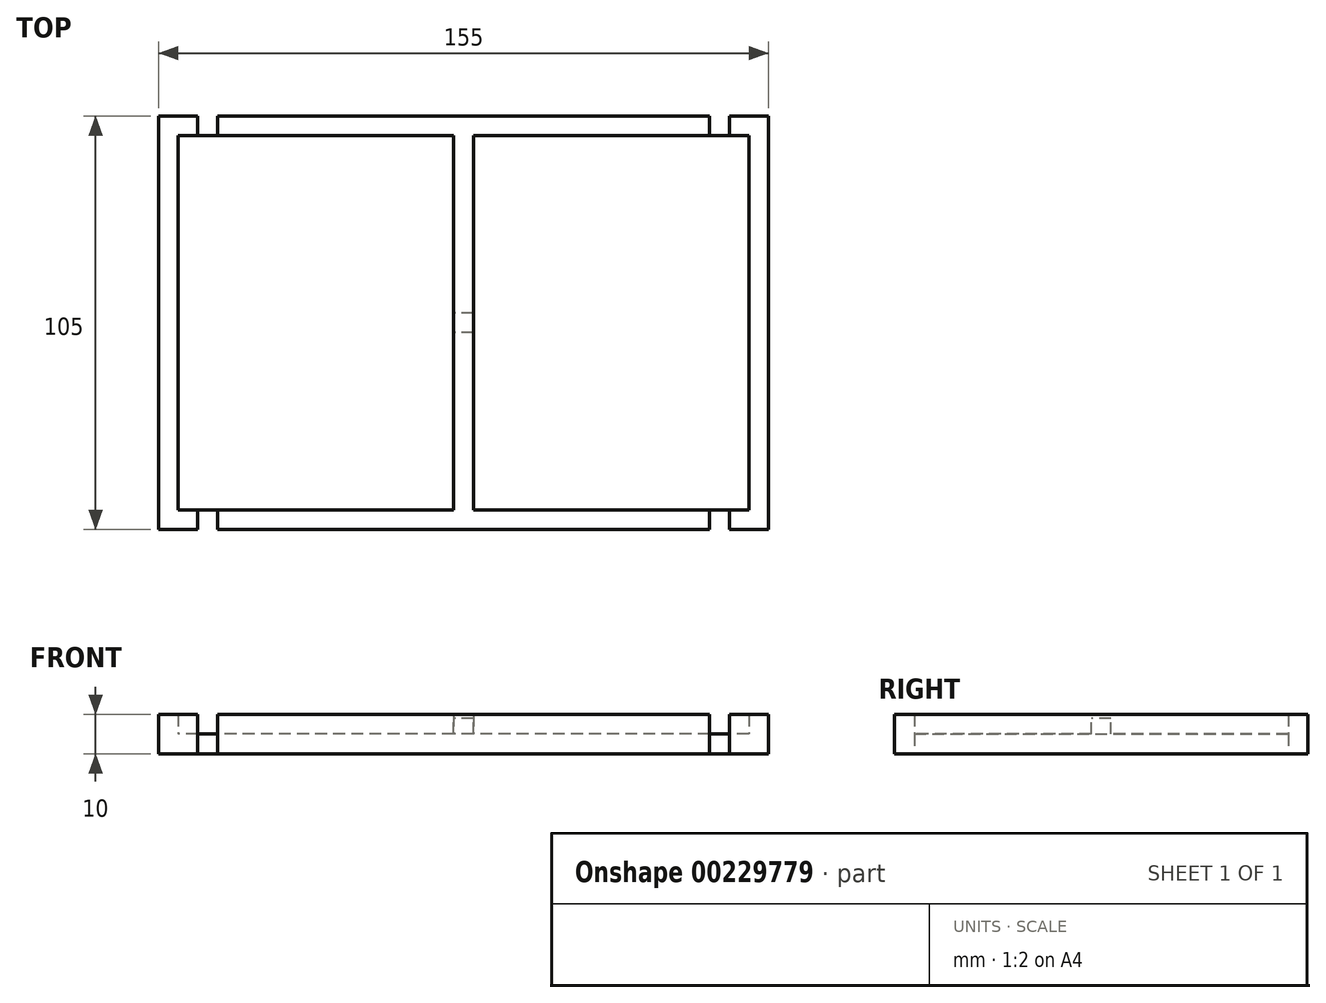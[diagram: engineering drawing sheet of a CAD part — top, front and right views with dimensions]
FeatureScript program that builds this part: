
annotation { "Feature Type Name" : "Feature", "Feature Type Description" : "" }
export const myFeature = defineFeature(function(context is Context, id is Id, definition is map)
    precondition{}
    {
        {
            var Q0;
            Q0=qCreatedBy(makeId("Top.planeOp"),FACE);
            var sketch = newSketch(context, id + "F0", { "sketchPlane" : qUnion([Q0])});
            skLineSegment(sketch, "E0.bottom", {"start": v(77.5, -52.5) * mm, "end": v(-77.5, -52.5) * mm});
            skLineSegment(sketch, "E0.top", {"start": v(77.5, 52.5) * mm, "end": v(-77.5, 52.5) * mm});
            skLineSegment(sketch, "E0.left", {"start": v(77.5, -52.5) * mm, "end": v(77.5, 52.5) * mm});
            skLineSegment(sketch, "E0.right", {"start": v(-77.5, -52.5) * mm, "end": v(-77.5, 52.5) * mm});
            skPoint(sketch, "E0.middle", {"position": v(0, 0) * mm});
            skLineSegment(sketch, "E1.bottom", {"start": v(2.5, -52.5) * mm, "end": v(-2.5, -52.5) * mm});
            skLineSegment(sketch, "E1.top", {"start": v(2.5, 52.5) * mm, "end": v(-2.5, 52.5) * mm});
            skLineSegment(sketch, "E1.left", {"start": v(2.5, -52.5) * mm, "end": v(2.5, 52.5) * mm});
            skLineSegment(sketch, "E1.right", {"start": v(-2.5, -52.5) * mm, "end": v(-2.5, 52.5) * mm});
            skSolve(sketch);
        }
        {
            var Q0;
            {var subQ0=sQuery(id+"F0.wireOp",EDGE,"E0.left");Q0=makeQuery(id+"F0.imprint","IMPRINT",FACE,{"disambiguationData":[TD([[makeQuery(id+"F0.imprint","IMPRINT",EDGE,{"derivedFrom":subQ0}),1.0]])]});}
            var Q1;
            {var subQ2=sQuery(id+"F0.wireOp",EDGE,"E0.right");Q1=makeQuery(id+"F0.imprint","IMPRINT",FACE,{"disambiguationData":[TD([[makeQuery(id+"F0.imprint","IMPRINT",EDGE,{"derivedFrom":subQ2}),-1.0]])]});}
            var Q2;
            {var subQ2=sQuery(id+"F0.wireOp",EDGE,"E1.left");Q2=makeQuery(id+"F0.imprint","IMPRINT",FACE,{"disambiguationData":[TD([[makeQuery(id+"F0.imprint","IMPRINT",EDGE,{"derivedFrom":subQ2}),1.0]])]});}
            extrude(context, id + "F1", {"entities" : qUnion([Q0, Q1, Q2]), "depth" : 10 * mm, "offsetDistance" : 25 * mm});
        }
        {
            var Q0;
            Q0=makeQuery(id+"F1.opExtrude","CAP_FACE",FACE,{"disambiguationData":[OSD([sQuery(id+"F0.wireOp",EDGE,"E0.bottom"),sQuery(id+"F0.wireOp",EDGE,"E0.top"),sQuery(id+"F0.wireOp",EDGE,"E0.left"),sQuery(id+"F0.wireOp",EDGE,"E0.right")])],"isStart":false});
            shell(context, id + "F2", {"entities" : qUnion([Q0]), "thickness" : 5 * mm});
        }
        {
            var Q0;
            Q0=qCreatedBy(makeId("Top.planeOp"),FACE);
            var sketch = newSketch(context, id + "F3", { "sketchPlane" : qUnion([Q0])});
            skLineSegment(sketch, "E2.bottom", {"start": v(-77.5, 52.5) * mm, "end": v(77.5, 52.5) * mm});
            skLineSegment(sketch, "E2.top", {"start": v(-77.5, -52.5) * mm, "end": v(77.5, -52.5) * mm});
            skLineSegment(sketch, "E2.left", {"start": v(-77.5, 52.5) * mm, "end": v(-77.5, -52.5) * mm});
            skLineSegment(sketch, "E2.right", {"start": v(77.5, 52.5) * mm, "end": v(77.5, -52.5) * mm});
            skLineSegment(sketch, "E3.bottom", {"start": v(-67.5, 52.5) * mm, "end": v(-62.5, 52.5) * mm});
            skLineSegment(sketch, "E3.top", {"start": v(-67.5, 47.5) * mm, "end": v(-62.5, 47.5) * mm});
            skLineSegment(sketch, "E3.left", {"start": v(-67.5, 52.5) * mm, "end": v(-67.5, 47.5) * mm});
            skLineSegment(sketch, "E3.right", {"start": v(-62.5, 52.5) * mm, "end": v(-62.5, 47.5) * mm});
            skLineSegment(sketch, "E4.0.1.0", {"start": v(-62.5, -47.5) * mm, "end": v(-62.5, -52.5) * mm});
            skLineSegment(sketch, "E4.0.1.1", {"start": v(-67.5, -47.5) * mm, "end": v(-67.5, -52.5) * mm});
            skLineSegment(sketch, "E4.0.1.2", {"start": v(-67.5, -52.5) * mm, "end": v(-62.5, -52.5) * mm});
            skLineSegment(sketch, "E4.direction2", {"start": v(-62.5, -47.5) * mm, "end": v(-62.5, -52.5) * mm, "construction": true});
            skPoint(sketch, "E5.orphan", {"position": v(67, 54) * mm});
            skLineSegment(sketch, "E6.MirrorCS", {"start": v(62.5, 52.5) * mm, "end": v(62.5, 47.5) * mm});
            skLineSegment(sketch, "E7.MirrorCS", {"start": v(67.5, 52.5) * mm, "end": v(67.5, 47.5) * mm});
            skLineSegment(sketch, "E8.MirrorCS", {"start": v(67.5, 52.5) * mm, "end": v(62.5, 52.5) * mm});
            skLineSegment(sketch, "E9.MirrorCS", {"start": v(67.5, 47.5) * mm, "end": v(62.5, 47.5) * mm});
            skLineSegment(sketch, "E10.MirrorCS", {"start": v(67.5, -47.5) * mm, "end": v(67.5, -52.5) * mm});
            skLineSegment(sketch, "E11", {"start": v(-67.5, -47.5) * mm, "end": v(-62.5, -47.5) * mm});
            skLineSegment(sketch, "E12.MirrorCS", {"start": v(67.5, -47.5) * mm, "end": v(62.5, -47.5) * mm});
            skLineSegment(sketch, "E13.MirrorCS", {"start": v(62.5, -47.5) * mm, "end": v(62.5, -52.5) * mm, "construction": true});
            skLineSegment(sketch, "E14", {"start": v(62.5, -47.5) * mm, "end": v(62.5, -52.5) * mm});
            skLineSegment(sketch, "E15", {"start": v(62.5, -52.5) * mm, "end": v(67.5, -52.5) * mm});
            skSolve(sketch);
        }
        {
            var Q0;
            {var subQ0=sQuery(id+"F3.wireOp",EDGE,"E2.left");Q0=makeQuery(id+"F3.imprint","IMPRINT",FACE,{"disambiguationData":[TD([[makeQuery(id+"F3.imprint","IMPRINT",EDGE,{"derivedFrom":subQ0}),1.0]])]});}
            extrude(context, id + "F4", {"entities" : qUnion([Q0]), "operationType" : NewBodyOperationType.INTERSECT, "depth" : 25 * mm, "offsetDistance" : 25 * mm});
        }
        {
            var Q0;
            {var subQ2=sQuery(id+"F0.wireOp",EDGE,"E1.left");Q0=makeQuery(id+"F0.imprint","IMPRINT",FACE,{"disambiguationData":[TD([[makeQuery(id+"F0.imprint","IMPRINT",EDGE,{"derivedFrom":subQ2}),1.0]])]});}
            extrude(context, id + "F5", {"entities" : qUnion([Q0]), "operationType" : NewBodyOperationType.ADD, "depth" : 10 * mm, "offsetDistance" : 25 * mm});
        }
        {
            var Q0;
            Q0=makeQuery(id+"F5.opExtrude","SWEPT_FACE",FACE,{"disambiguationData":[OSD([sQuery(id+"F0.wireOp",EDGE,"E1.right")])]});
            var sketch = newSketch(context, id + "F6", { "sketchPlane" : qUnion([Q0])});
            skLineSegment(sketch, "E16.bottom", {"start": v(-47.5, 10) * mm, "end": v(47.5, 10) * mm});
            skLineSegment(sketch, "E16.top", {"start": v(-47.5, 5) * mm, "end": v(47.5, 5) * mm});
            skLineSegment(sketch, "E16.left", {"start": v(-47.5, 10) * mm, "end": v(-47.5, 5) * mm});
            skLineSegment(sketch, "E16.right", {"start": v(47.5, 10) * mm, "end": v(47.5, 5) * mm});
            skLineSegment(sketch, "E17", {"start": v(0, 10) * mm, "end": v(0, 5) * mm});
            skLineSegment(sketch, "E18.bottom", {"start": v(-2.5, 5) * mm, "end": v(2.5, 5) * mm});
            skLineSegment(sketch, "E18.top", {"start": v(-2.5, 9) * mm, "end": v(2.5, 9) * mm});
            skLineSegment(sketch, "E18.left", {"start": v(-2.5, 5) * mm, "end": v(-2.5, 9) * mm});
            skLineSegment(sketch, "E18.right", {"start": v(2.5, 5) * mm, "end": v(2.5, 9) * mm});
            skPoint(sketch, "E19", {"position": v(0, 9) * mm});
            skSolve(sketch);
        }
        {
            var Q0;
            {var subQ5=sQuery(id+"F6.wireOp",EDGE,"E18.left");Q0=makeQuery(id+"F6.imprint","IMPRINT",FACE,{"disambiguationData":[TD([[makeQuery(id+"F6.imprint","IMPRINT",EDGE,{"derivedFrom":subQ5}),-1.0]])]});}
            var Q1;
            {var subQ5=sQuery(id+"F6.wireOp",EDGE,"E18.right");Q1=makeQuery(id+"F6.imprint","IMPRINT",FACE,{"disambiguationData":[TD([[makeQuery(id+"F6.imprint","IMPRINT",EDGE,{"derivedFrom":subQ5}),1.0]])]});}
            extrude(context, id + "F7", {"entities" : qUnion([Q0, Q1]), "operationType" : NewBodyOperationType.REMOVE, "oppositeDirection" : true, "depth" : 25 * mm, "offsetDistance" : 25 * mm});
        }
    });
